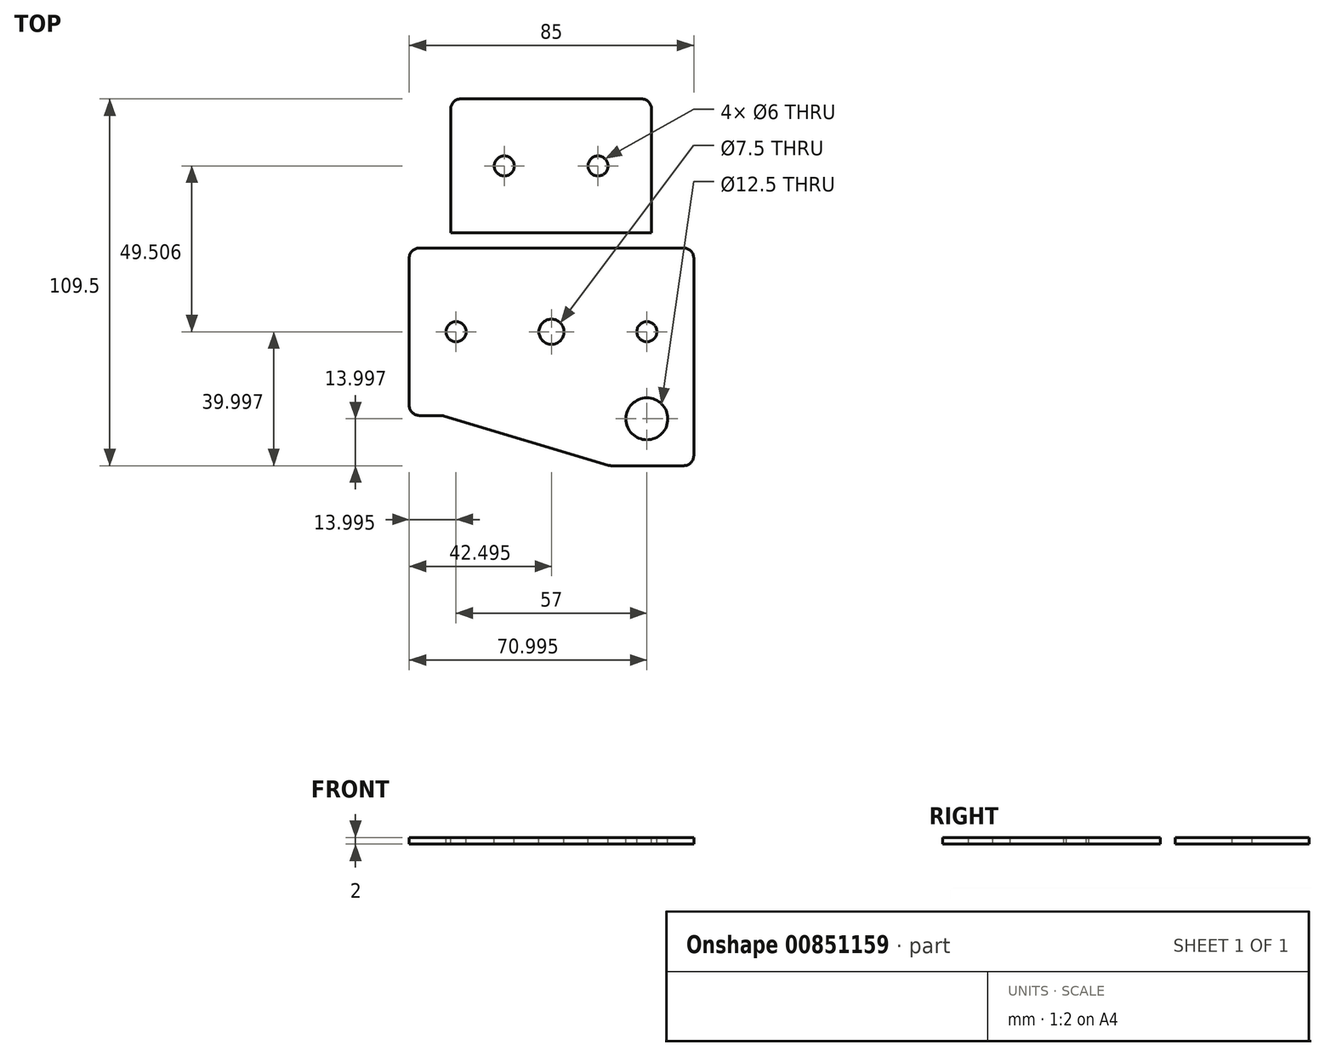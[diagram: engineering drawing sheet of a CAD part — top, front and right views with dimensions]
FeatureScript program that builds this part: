
annotation { "Feature Type Name" : "Feature", "Feature Type Description" : "" }
export const myFeature = defineFeature(function(context is Context, id is Id, definition is map)
    precondition{}
    {
        {
            var Q0;
            Q0=qCreatedBy(makeId("Top.planeOp"),FACE);
            var sketch = newSketch(context, id + "F0", { "sketchPlane" : qUnion([Q0])});
            skLineSegment(sketch, "E0", {"start": v(-51.84, -33.87) * mm, "end": v(33.16, -33.87) * mm});
            skLineSegment(sketch, "E1.bottom", {"start": v(-51.84, -0.56) * mm, "end": v(33.16, -0.56) * mm});
            skLineSegment(sketch, "E1.top", {"start": v(-51.84, -65.56) * mm, "end": v(33.16, -65.56) * mm});
            skLineSegment(sketch, "E1.left", {"start": v(-51.84, -0.56) * mm, "end": v(-51.84, -65.56) * mm});
            skLineSegment(sketch, "E1.right", {"start": v(33.16, -0.56) * mm, "end": v(33.16, -65.56) * mm});
            skLineSegment(sketch, "E2.bottom", {"start": v(-39.45, 3.94) * mm, "end": v(20.55, 3.94) * mm});
            skLineSegment(sketch, "E2.top", {"start": v(-39.45, 43.94) * mm, "end": v(20.55, 43.94) * mm});
            skLineSegment(sketch, "E2.left", {"start": v(-39.45, 3.94) * mm, "end": v(-39.45, 43.94) * mm});
            skLineSegment(sketch, "E2.right", {"start": v(20.55, 3.94) * mm, "end": v(20.55, 43.94) * mm});
            skCircle(sketch, "E3", {"center": v(-23.45, 23.94) * mm, "radius": 3 * mm});
            skCircle(sketch, "E4", {"center": v(4.55, 23.94) * mm, "radius": 3 * mm});
            skCircle(sketch, "E5", {"center": v(-37.84, -25.56) * mm, "radius": 3 * mm});
            skCircle(sketch, "E6", {"center": v(-9.34, -25.56) * mm, "radius": 3.75 * mm});
            skCircle(sketch, "E7", {"center": v(19.16, -25.56) * mm, "radius": 3 * mm});
            skCircle(sketch, "E8", {"center": v(19.16, -51.56) * mm, "radius": 6.25 * mm});
            skLineSegment(sketch, "E9", {"start": v(-41.93, -50.56) * mm, "end": v(-51.84, -50.56) * mm});
            skLineSegment(sketch, "E10", {"start": v(-41.93, -50.56) * mm, "end": v(8.16, -65.56) * mm});
            skSolve(sketch);
        }
        {
            var Q0;
            Q0=makeQuery(id+"F0.imprint","IMPRINT",FACE,{"disambiguationData":[TD([[makeQuery(id+"F0.imprint","IMPRINT",EDGE,{"derivedFrom":sQuery(id+"F0.wireOp",EDGE,"E2.bottom")}),1.0]])]});
            var Q1;
            {var subQ1=sQuery(id+"F0.wireOp",EDGE,"E0");Q1=makeQuery(id+"F0.imprint","IMPRINT",FACE,{"disambiguationData":[TD([[makeQuery(id+"F0.imprint","IMPRINT",EDGE,{"derivedFrom":subQ1}),-1.0]])]});}
            var Q2;
            {var subQ1=sQuery(id+"F0.wireOp",EDGE,"E0");Q2=makeQuery(id+"F0.imprint","IMPRINT",FACE,{"disambiguationData":[TD([[makeQuery(id+"F0.imprint","IMPRINT",EDGE,{"derivedFrom":subQ1}),1.0]])]});}
            extrude(context, id + "F1", {"entities" : qUnion([Q0, Q1, Q2]), "oppositeDirection" : true, "depth" : 2 * mm, "offsetDistance" : 25 * mm});
        }
        {
            var Q0;
            Q0=makeQuery(id+"F1.opExtrude","SWEPT_EDGE",EDGE,{"disambiguationData":[OSD([sQuery(id+"F0.wireOp",EDGE,"E2.top"),sQuery(id+"F0.wireOp",EDGE,"E2.left")])]});
            var Q1;
            Q1=makeQuery(id+"F1.opExtrude","SWEPT_EDGE",EDGE,{"disambiguationData":[OSD([sQuery(id+"F0.wireOp",EDGE,"E2.top"),sQuery(id+"F0.wireOp",EDGE,"E2.right")])]});
            var Q2;
            Q2=makeQuery(id+"F1.opExtrude","SWEPT_EDGE",EDGE,{"disambiguationData":[OSD([sQuery(id+"F0.wireOp",EDGE,"E1.bottom"),sQuery(id+"F0.wireOp",EDGE,"E1.left")])]});
            var Q3;
            Q3=makeQuery(id+"F1.opExtrude","SWEPT_EDGE",EDGE,{"disambiguationData":[OSD([sQuery(id+"F0.wireOp",EDGE,"E1.left"),sQuery(id+"F0.wireOp",EDGE,"E9")])]});
            var Q4;
            Q4=makeQuery(id+"F1.opExtrude","SWEPT_EDGE",EDGE,{"disambiguationData":[OSD([sQuery(id+"F0.wireOp",EDGE,"E9"),sQuery(id+"F0.wireOp",EDGE,"E10")])]});
            var Q5;
            Q5=makeQuery(id+"F1.opExtrude","SWEPT_EDGE",EDGE,{"disambiguationData":[OSD([sQuery(id+"F0.wireOp",EDGE,"E1.top"),sQuery(id+"F0.wireOp",EDGE,"E10")])]});
            var Q6;
            Q6=makeQuery(id+"F1.opExtrude","SWEPT_EDGE",EDGE,{"disambiguationData":[OSD([sQuery(id+"F0.wireOp",EDGE,"E1.top"),sQuery(id+"F0.wireOp",EDGE,"E1.right")])]});
            var Q7;
            Q7=makeQuery(id+"F1.opExtrude","SWEPT_EDGE",EDGE,{"disambiguationData":[OSD([sQuery(id+"F0.wireOp",EDGE,"E1.bottom"),sQuery(id+"F0.wireOp",EDGE,"E1.right")])]});
            fillet(context, id + "F2", {"entities" : qUnion([Q0, Q1, Q2, Q3, Q4, Q5, Q6, Q7]), "radius" : 3 * mm, "tangentPropagation" : true, "allowEdgeOverflow" : false});
        }
    });
